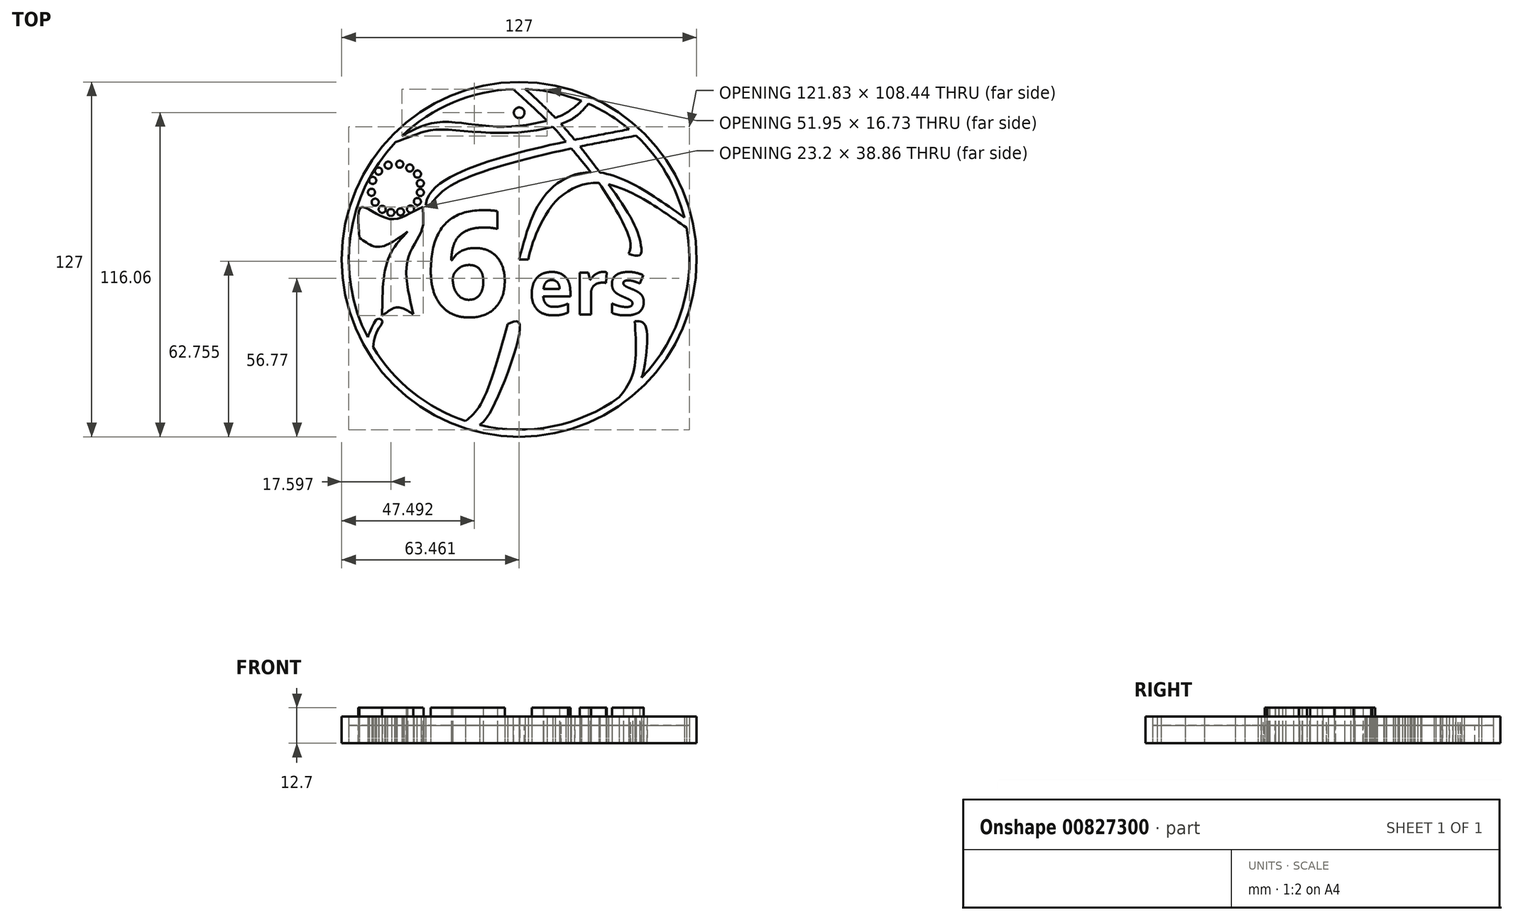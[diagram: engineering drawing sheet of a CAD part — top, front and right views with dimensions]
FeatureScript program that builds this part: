
annotation { "Feature Type Name" : "Feature", "Feature Type Description" : "" }
export const myFeature = defineFeature(function(context is Context, id is Id, definition is map)
    precondition{}
    {
        {
            var Q0;
            Q0=qCreatedBy(makeId("Top.planeOp"),FACE);
            var sketch = newSketch(context, id + "F0", { "sketchPlane" : qUnion([Q0])});
            skCircle(sketch, "E0", {"center": v(0, 0) * mm, "radius": 63.5 * mm});
            skCircle(sketch, "E1", {"center": v(0, 0) * mm, "radius": 60.96 * mm});
            skFitSpline(sketch, "E2", {"points": [v(-54.2, -27.9) * mm, v(-52.23, -23.42) * mm, v(-50.53, -21.33) * mm, v(-49.01, -22.09) * mm, v(-50.72, -25.5) * mm, v(-52.26, -31.38) * mm], "startDerivative": vector(8.28, 20.2) * mm, "endDerivative": vector(-3.3, -23.9) * mm});
            skFitSpline(sketch, "E3", {"points": [v(-49.01, -20.18) * mm, v(-43.9, -17.16) * mm, v(-37.82, -19.62) * mm], "startDerivative": vector(10.4, 7.01) * mm, "endDerivative": vector(11.94, -7.2) * mm});
            skFitSpline(sketch, "E4", {"points": [v(-37.82, -19.62) * mm, v(-39.86, 0) * mm, v(-34.6, 11.28) * mm, v(-34.47, 18.69) * mm], "startDerivative": vector(-12.1, 50.15) * mm, "endDerivative": vector(0.96, 26.71) * mm});
            skFitSpline(sketch, "E5", {"points": [v(-34.47, 18.69) * mm, v(-46.5, 14.5) * mm, v(-56.48, 18.69) * mm, v(-57.22, 7.7) * mm], "startDerivative": vector(-38.35, -14.44) * mm, "endDerivative": vector(0.93, -47.09) * mm});
            skFitSpline(sketch, "E6", {"points": [v(-57.22, 7.7) * mm, v(-50.53, 4.46) * mm, v(-39.86, 9.95) * mm], "startDerivative": vector(14.43, -9.54) * mm, "endDerivative": vector(19.87, 14.21) * mm});
            skFitSpline(sketch, "E7", {"points": [v(-39.86, 9.95) * mm, v(-46.93, 0) * mm, v(-49.01, -20.18) * mm], "startDerivative": vector(-18.63, -19.86) * mm, "endDerivative": vector(-0.32, -38.2) * mm});
            skCircle(sketch, "E8", {"center": v(-42.48, 17) * mm, "radius": 1.27 * mm});
            skCircle(sketch, "E9", {"center": v(-38.87, 18.01) * mm, "radius": 1.27 * mm});
            skCircle(sketch, "E10", {"center": v(-36.4, 20.69) * mm, "radius": 1.27 * mm});
            skCircle(sketch, "E11", {"center": v(-35.38, 23.93) * mm, "radius": 1.27 * mm});
            skCircle(sketch, "E12", {"center": v(-35.38, 27.2) * mm, "radius": 1.27 * mm});
            skCircle(sketch, "E13", {"center": v(-36.4, 30.53) * mm, "radius": 1.27 * mm});
            skCircle(sketch, "E14", {"center": v(-39.15, 32.7) * mm, "radius": 1.27 * mm});
            skCircle(sketch, "E15", {"center": v(-42.73, 34.07) * mm, "radius": 1.27 * mm});
            skCircle(sketch, "E16", {"center": v(-46.86, 33.7) * mm, "radius": 1.27 * mm});
            skCircle(sketch, "E17", {"center": v(-50.3, 31.59) * mm, "radius": 1.27 * mm});
            skCircle(sketch, "E18", {"center": v(-52.42, 28.24) * mm, "radius": 1.27 * mm});
            skCircle(sketch, "E19", {"center": v(-52.85, 23.99) * mm, "radius": 1.27 * mm});
            skCircle(sketch, "E20", {"center": v(-51.53, 20.48) * mm, "radius": 1.27 * mm});
            skCircle(sketch, "E21", {"center": v(-49, 17.9) * mm, "radius": 1.27 * mm});
            skCircle(sketch, "E22", {"center": v(-45.92, 16.77) * mm, "radius": 1.27 * mm});
            skPoint(sketch, "E23", {"position": v(-16.13, 18.69) * mm});
            skPoint(sketch, "E24", {"position": v(-16.13, -20.18) * mm});
            skText(sketch, "E25", { "text": "6", "fontName": "OpenSans-Bold.ttf"});
            skText(sketch, "E26", { "text": "ers", "fontName": "OpenSans-Bold.ttf"});
            skFitSpline(sketch, "E27", {"points": [v(-31.72, 19.4) * mm, v(-15.34, 30.53) * mm, v(41.92, 44.25) * mm], "startDerivative": vector(25.64, 42.91) * mm, "endDerivative": vector(102.82, 18.21) * mm});
            skFitSpline(sketch, "E28", {"points": [v(-33.46, 19.4) * mm, v(-22.43, 30.53) * mm, v(6.43, 39.84) * mm, v(39.36, 46.55) * mm], "startDerivative": vector(8.52, 60) * mm, "endDerivative": vector(83.39, 15.7) * mm});
            skFitSpline(sketch, "E29", {"points": [v(-41.99, 44.2) * mm, v(-28.87, 49.08) * mm, v(-7.34, 47.48) * mm, v(14.98, 51.47) * mm, v(22.29, 56.74) * mm], "startDerivative": vector(52.87, 28.6) * mm, "endDerivative": vector(31.88, 29.74) * mm});
            skFitSpline(sketch, "E30", {"points": [v(-44.2, 41.97) * mm, v(-37.5, 44.52) * mm, v(-29.62, 46.43) * mm, v(-7.1, 45.23) * mm, v(17.47, 49.47) * mm, v(24.76, 55.7) * mm], "startDerivative": vector(46.42, 16.58) * mm, "endDerivative": vector(33.1, 40.53) * mm});
            skFitSpline(sketch, "E31", {"points": [v(0, 0) * mm, v(9.53, 23.28) * mm, v(28.02, 31.17) * mm, v(59.1, 14.98) * mm], "startDerivative": vector(20.8, 79.75) * mm, "endDerivative": vector(83.63, -59.85) * mm});
            skFitSpline(sketch, "E32", {"points": [v(3.26, 0) * mm, v(5.48, 7.5) * mm, v(13.6, 21.25) * mm, v(28.47, 27.34) * mm, v(47.19, 19.9) * mm, v(59.9, 11.32) * mm], "startDerivative": vector(9.3, 47.2) * mm, "endDerivative": vector(57.56, -41.12) * mm});
            skFitSpline(sketch, "E33", {"points": [v(0, 0) * mm, v(3.26, 0) * mm], "startDerivative": vector(3.54, 0) * mm, "endDerivative": vector(3.54, 0) * mm});
            skFitSpline(sketch, "E34", {"points": [v(-33.46, 19.4) * mm, v(-31.72, 19.4) * mm], "startDerivative": vector(1.74, 0) * mm, "endDerivative": vector(1.74, 0) * mm});
            skFitSpline(sketch, "E35", {"points": [v(35.83, -49.32) * mm, v(40.75, -40.8) * mm, v(41.39, -22.1) * mm], "startDerivative": vector(13.93, 17.74) * mm, "endDerivative": vector(-1.97, 35.73) * mm});
            skFitSpline(sketch, "E36", {"points": [v(43.8, -42.4) * mm, v(44.74, -38.89) * mm, v(45.05, -23.58) * mm, v(41.39, -22.1) * mm], "startDerivative": vector(3.64, 9.81) * mm, "endDerivative": vector(-17.03, 0.06) * mm});
            skFitSpline(sketch, "E37", {"points": [v(39.16, 1.93) * mm, v(39.63, 6.7) * mm, v(28.47, 27.34) * mm, v(18.66, 39.7) * mm, v(12.06, 47.5) * mm, v(-2.14, 60.92) * mm], "startDerivative": vector(11.87, 33.04) * mm, "endDerivative": vector(-66.74, 59.9) * mm});
            skFitSpline(sketch, "E38", {"points": [v(2.14, 60.92) * mm, v(6.47, 57.09) * mm, v(14.98, 48.42) * mm, v(21.77, 40.37) * mm, v(32, 26.84) * mm, v(41.07, 12.77) * mm, v(43.46, 5.6) * mm, v(43.3, 1.6) * mm, v(39.16, 1.93) * mm], "startDerivative": vector(39.37, -33.43) * mm, "endDerivative": vector(-60.68, 17.03) * mm});
            skFitSpline(sketch, "E39", {"points": [v(-19.17, -57.87) * mm, v(-13.98, -52.18) * mm, v(-4.12, -23.17) * mm], "startDerivative": vector(15.65, 12.5) * mm, "endDerivative": vector(14.54, 52.37) * mm});
            skFitSpline(sketch, "E40", {"points": [v(-14.15, -59.3) * mm, v(-9.8, -53.7) * mm, v(0, -22.8) * mm, v(-4.12, -23.17) * mm], "startDerivative": vector(14.17, 11.52) * mm, "endDerivative": vector(-26.92, -12.48) * mm});
            const initialGuessF0  = {"E25": [-0.03346, -0.02029, 1, 0, 0.0378], "E26": [0.00326, -0.01978, 1, 0, 0.01978]};
            skSetInitialGuess(sketch, initialGuessF0);
            skSolve(sketch);
        }
        {
            var Q0;
            Q0=makeQuery(id+"F0.imprint","IMPRINT",FACE,{"disambiguationData":[TD([[makeQuery(id+"F0.imprint","IMPRINT",EDGE,{"derivedFrom":sQuery(id+"F0.wireOp",EDGE,"E0")}),1.0]])]});
            var Q1;
            Q1=makeQuery(id+"F0.imprint","IMPRINT",FACE,{"disambiguationData":[TD([[makeQuery(id+"F0.imprint","IMPRINT",EDGE,{"derivedFrom":sQuery(id+"F0.wireOp",EDGE,"E8")}),1.0]])]});
            var Q2;
            Q2=makeQuery(id+"F0.imprint","IMPRINT",FACE,{"disambiguationData":[TD([[makeQuery(id+"F0.imprint","IMPRINT",EDGE,{"derivedFrom":sQuery(id+"F0.wireOp",EDGE,"E9")}),1.0]])]});
            var Q3;
            Q3=makeQuery(id+"F0.imprint","IMPRINT",FACE,{"disambiguationData":[TD([[makeQuery(id+"F0.imprint","IMPRINT",EDGE,{"derivedFrom":sQuery(id+"F0.wireOp",EDGE,"E11")}),1.0]])]});
            var Q4;
            Q4=makeQuery(id+"F0.imprint","IMPRINT",FACE,{"disambiguationData":[TD([[makeQuery(id+"F0.imprint","IMPRINT",EDGE,{"derivedFrom":sQuery(id+"F0.wireOp",EDGE,"E10")}),1.0]])]});
            var Q5;
            Q5=makeQuery(id+"F0.imprint","IMPRINT",FACE,{"disambiguationData":[TD([[makeQuery(id+"F0.imprint","IMPRINT",EDGE,{"derivedFrom":sQuery(id+"F0.wireOp",EDGE,"E12")}),1.0]])]});
            var Q6;
            Q6=makeQuery(id+"F0.imprint","IMPRINT",FACE,{"disambiguationData":[TD([[makeQuery(id+"F0.imprint","IMPRINT",EDGE,{"derivedFrom":sQuery(id+"F0.wireOp",EDGE,"E13")}),1.0]])]});
            var Q7;
            Q7=makeQuery(id+"F0.imprint","IMPRINT",FACE,{"disambiguationData":[TD([[makeQuery(id+"F0.imprint","IMPRINT",EDGE,{"derivedFrom":sQuery(id+"F0.wireOp",EDGE,"E14")}),1.0]])]});
            var Q8;
            Q8=makeQuery(id+"F0.imprint","IMPRINT",FACE,{"disambiguationData":[TD([[makeQuery(id+"F0.imprint","IMPRINT",EDGE,{"derivedFrom":sQuery(id+"F0.wireOp",EDGE,"E15")}),1.0]])]});
            var Q9;
            Q9=makeQuery(id+"F0.imprint","IMPRINT",FACE,{"disambiguationData":[TD([[makeQuery(id+"F0.imprint","IMPRINT",EDGE,{"derivedFrom":sQuery(id+"F0.wireOp",EDGE,"E16")}),1.0]])]});
            var Q10;
            Q10=makeQuery(id+"F0.imprint","IMPRINT",FACE,{"disambiguationData":[TD([[makeQuery(id+"F0.imprint","IMPRINT",EDGE,{"derivedFrom":sQuery(id+"F0.wireOp",EDGE,"E17")}),1.0]])]});
            var Q11;
            Q11=makeQuery(id+"F0.imprint","IMPRINT",FACE,{"disambiguationData":[TD([[makeQuery(id+"F0.imprint","IMPRINT",EDGE,{"derivedFrom":sQuery(id+"F0.wireOp",EDGE,"E18")}),1.0]])]});
            var Q12;
            Q12=makeQuery(id+"F0.imprint","IMPRINT",FACE,{"disambiguationData":[TD([[makeQuery(id+"F0.imprint","IMPRINT",EDGE,{"derivedFrom":sQuery(id+"F0.wireOp",EDGE,"E19")}),1.0]])]});
            var Q13;
            Q13=makeQuery(id+"F0.imprint","IMPRINT",FACE,{"disambiguationData":[TD([[makeQuery(id+"F0.imprint","IMPRINT",EDGE,{"derivedFrom":sQuery(id+"F0.wireOp",EDGE,"E20")}),1.0]])]});
            var Q14;
            Q14=makeQuery(id+"F0.imprint","IMPRINT",FACE,{"disambiguationData":[TD([[makeQuery(id+"F0.imprint","IMPRINT",EDGE,{"derivedFrom":sQuery(id+"F0.wireOp",EDGE,"E21")}),1.0]])]});
            var Q15;
            Q15=makeQuery(id+"F0.imprint","IMPRINT",FACE,{"disambiguationData":[TD([[makeQuery(id+"F0.imprint","IMPRINT",EDGE,{"derivedFrom":sQuery(id+"F0.wireOp",EDGE,"E22")}),1.0]])]});
            var Q16;
            {var subQ0=sQuery(id+"F0.wireOp",EDGE,"E34");Q16=makeQuery(id+"F0.imprint","IMPRINT",FACE,{"disambiguationData":[TD([[makeQuery(id+"F0.imprint","IMPRINT",EDGE,{"derivedFrom":subQ0}),1.0]])]});}
            var Q17;
            {var subQ0=sQuery(id+"F0.wireOp",EDGE,"E29");var subQ1=sQuery(id+"F0.wireOp",EDGE,"E1");var subQ2=makeQuery(id+"F0.imprint","INTERSECT",VERTEX,{"disambiguationData":[OD(0.0)],"derivedFrom":[subQ1,subQ0]});Q17=makeQuery(id+"F0.imprint","IMPRINT",FACE,{"disambiguationData":[TD([[makeQuery(id+"F0.imprint","IMPRINT",EDGE,{"disambiguationData":[TD([[subQ2,-1.0]])],"derivedFrom":subQ1}),1.0]])]});}
            var Q18;
            {var subQ0=sQuery(id+"F0.wireOp",EDGE,"E37");var subQ1=sQuery(id+"F0.wireOp",EDGE,"E29");var subQ2=makeQuery(id+"F0.imprint","INTERSECT",VERTEX,{"derivedFrom":[subQ1,subQ0]});Q18=makeQuery(id+"F0.imprint","IMPRINT",FACE,{"disambiguationData":[TD([[makeQuery(id+"F0.imprint","IMPRINT",EDGE,{"disambiguationData":[TD([[subQ2,-1.0]])],"derivedFrom":subQ1}),-1.0]])]});}
            var Q19;
            {var subQ0=sQuery(id+"F0.wireOp",EDGE,"E37");var subQ1=sQuery(id+"F0.wireOp",EDGE,"E1");var subQ2=makeQuery(id+"F0.imprint","INTERSECT",VERTEX,{"derivedFrom":[subQ1,subQ0]});Q19=makeQuery(id+"F0.imprint","IMPRINT",FACE,{"disambiguationData":[TD([[makeQuery(id+"F0.imprint","IMPRINT",EDGE,{"disambiguationData":[TD([[subQ2,1.0]])],"derivedFrom":subQ1}),1.0]])]});}
            var Q20;
            {var subQ0=sQuery(id+"F0.wireOp",EDGE,"E29");var subQ1=sQuery(id+"F0.wireOp",EDGE,"E1");var subQ2=makeQuery(id+"F0.imprint","INTERSECT",VERTEX,{"disambiguationData":[OD(1.0)],"derivedFrom":[subQ1,subQ0]});Q20=makeQuery(id+"F0.imprint","IMPRINT",FACE,{"disambiguationData":[TD([[makeQuery(id+"F0.imprint","IMPRINT",EDGE,{"disambiguationData":[TD([[subQ2,1.0]])],"derivedFrom":subQ1}),1.0]])]});}
            var Q21;
            {var subQ0=sQuery(id+"F0.wireOp",EDGE,"E37");var subQ1=sQuery(id+"F0.wireOp",EDGE,"E28");var subQ2=makeQuery(id+"F0.imprint","INTERSECT",VERTEX,{"derivedFrom":[subQ1,subQ0]});Q21=makeQuery(id+"F0.imprint","IMPRINT",FACE,{"disambiguationData":[TD([[makeQuery(id+"F0.imprint","IMPRINT",EDGE,{"disambiguationData":[TD([[subQ2,-1.0]])],"derivedFrom":subQ1}),1.0]])]});}
            var Q22;
            {var subQ0=sQuery(id+"F0.wireOp",EDGE,"E37");var subQ1=sQuery(id+"F0.wireOp",EDGE,"E27");var subQ2=makeQuery(id+"F0.imprint","INTERSECT",VERTEX,{"derivedFrom":[subQ1,subQ0]});Q22=makeQuery(id+"F0.imprint","IMPRINT",FACE,{"disambiguationData":[TD([[makeQuery(id+"F0.imprint","IMPRINT",EDGE,{"disambiguationData":[TD([[subQ2,-1.0]])],"derivedFrom":subQ1}),1.0]])]});}
            var Q23;
            {var subQ0=sQuery(id+"F0.wireOp",EDGE,"E27");var subQ1=sQuery(id+"F0.wireOp",EDGE,"E1");var subQ2=makeQuery(id+"F0.imprint","INTERSECT",VERTEX,{"derivedFrom":[subQ1,subQ0]});Q23=makeQuery(id+"F0.imprint","IMPRINT",FACE,{"disambiguationData":[TD([[makeQuery(id+"F0.imprint","IMPRINT",EDGE,{"disambiguationData":[TD([[subQ2,-1.0]])],"derivedFrom":subQ1}),1.0]])]});}
            var Q24;
            {var subQ0=sQuery(id+"F0.wireOp",EDGE,"E37");var subQ1=sQuery(id+"F0.wireOp",EDGE,"E27");var subQ2=makeQuery(id+"F0.imprint","INTERSECT",VERTEX,{"derivedFrom":[subQ1,subQ0]});Q24=makeQuery(id+"F0.imprint","IMPRINT",FACE,{"disambiguationData":[TD([[makeQuery(id+"F0.imprint","IMPRINT",EDGE,{"disambiguationData":[TD([[subQ2,-1.0]])],"derivedFrom":subQ1}),-1.0]])]});}
            var Q25;
            {var subQ0=sQuery(id+"F0.wireOp",EDGE,"E37");var subQ1=sQuery(id+"F0.wireOp",EDGE,"E31");var subQ2=makeQuery(id+"F0.imprint","INTERSECT",VERTEX,{"derivedFrom":[subQ1,subQ0]});Q25=makeQuery(id+"F0.imprint","IMPRINT",FACE,{"disambiguationData":[TD([[makeQuery(id+"F0.imprint","IMPRINT",EDGE,{"disambiguationData":[TD([[subQ2,-1.0]])],"derivedFrom":subQ1}),-1.0]])]});}
            var Q26;
            {var subQ0=sQuery(id+"F0.wireOp",EDGE,"E31");var subQ1=sQuery(id+"F0.wireOp",EDGE,"E1");var subQ2=makeQuery(id+"F0.imprint","INTERSECT",VERTEX,{"derivedFrom":[subQ1,subQ0]});Q26=makeQuery(id+"F0.imprint","IMPRINT",FACE,{"disambiguationData":[TD([[makeQuery(id+"F0.imprint","IMPRINT",EDGE,{"disambiguationData":[TD([[subQ2,1.0]])],"derivedFrom":subQ1}),1.0]])]});}
            var Q27;
            {var subQ0=sQuery(id+"F0.wireOp",EDGE,"E33");Q27=makeQuery(id+"F0.imprint","IMPRINT",FACE,{"disambiguationData":[TD([[makeQuery(id+"F0.imprint","IMPRINT",EDGE,{"derivedFrom":subQ0}),1.0]])]});}
            var Q28;
            {var subQ0=sQuery(id+"F0.wireOp",EDGE,"E2");Q28=makeQuery(id+"F0.imprint","IMPRINT",FACE,{"disambiguationData":[TD([[makeQuery(id+"F0.imprint","IMPRINT",EDGE,{"derivedFrom":subQ0}),-1.0]])]});}
            var Q29;
            {var subQ0=sQuery(id+"F0.wireOp",EDGE,"E39");Q29=makeQuery(id+"F0.imprint","IMPRINT",FACE,{"disambiguationData":[TD([[makeQuery(id+"F0.imprint","IMPRINT",EDGE,{"derivedFrom":subQ0}),-1.0]])]});}
            var Q30;
            {var subQ0=sQuery(id+"F0.wireOp",EDGE,"E35");Q30=makeQuery(id+"F0.imprint","IMPRINT",FACE,{"disambiguationData":[TD([[makeQuery(id+"F0.imprint","IMPRINT",EDGE,{"derivedFrom":subQ0}),-1.0]])]});}
            var Q31;
            {var subQ0=sQuery(id+"F0.wireOp",EDGE,"E37");var subQ1=sQuery(id+"F0.wireOp",EDGE,"E32");var subQ2=makeQuery(id+"F0.imprint","INTERSECT",VERTEX,{"derivedFrom":[subQ1,subQ0]});Q31=makeQuery(id+"F0.imprint","IMPRINT",FACE,{"disambiguationData":[TD([[makeQuery(id+"F0.imprint","IMPRINT",EDGE,{"disambiguationData":[TD([[subQ2,-1.0]])],"derivedFrom":subQ1}),-1.0]])]});}
            extrude(context, id + "F1", {"entities" : qUnion([Q0, Q1, Q2, Q3, Q4, Q5, Q6, Q7, Q8, Q9, Q10, Q11, Q12, Q13, Q14, Q15, Q16, Q17, Q18, Q19, Q20, Q21, Q22, Q23, Q24, Q25, Q26, Q27, Q28, Q29, Q30, Q31]), "depth" : 9.52 * mm, "offsetDistance" : 25.4 * mm});
        }
        {
            var Q0;
            Q0=makeQuery(id+"F0.imprint","IMPRINT",FACE,{"disambiguationData":[TD([[makeQuery(id+"F0.imprint","IMPRINT",EDGE,{"derivedFrom":sQuery(id+"F0.wireOp",EDGE,"E25.sketch_text.stroke-17")}),1.0]])]});
            var Q1;
            {var subQ6=sQuery(id+"F0.wireOp",EDGE,"E2");Q1=makeQuery(id+"F0.imprint","IMPRINT",FACE,{"disambiguationData":[TD([[makeQuery(id+"F0.imprint","IMPRINT",EDGE,{"derivedFrom":subQ6}),1.0]])]});}
            var Q2;
            {var subQ0=sQuery(id+"F0.wireOp",EDGE,"E27");var subQ1=sQuery(id+"F0.wireOp",EDGE,"E1");var subQ2=makeQuery(id+"F0.imprint","INTERSECT",VERTEX,{"derivedFrom":[subQ1,subQ0]});Q2=makeQuery(id+"F0.imprint","IMPRINT",FACE,{"disambiguationData":[TD([[makeQuery(id+"F0.imprint","IMPRINT",EDGE,{"disambiguationData":[TD([[subQ2,1.0]])],"derivedFrom":subQ1}),1.0]])]});}
            var Q3;
            {var subQ0=sQuery(id+"F0.wireOp",EDGE,"E28");var subQ1=sQuery(id+"F0.wireOp",EDGE,"E1");var subQ2=makeQuery(id+"F0.imprint","INTERSECT",VERTEX,{"derivedFrom":[subQ1,subQ0]});Q3=makeQuery(id+"F0.imprint","IMPRINT",FACE,{"disambiguationData":[TD([[makeQuery(id+"F0.imprint","IMPRINT",EDGE,{"disambiguationData":[TD([[subQ2,-1.0]])],"derivedFrom":subQ1}),1.0]])]});}
            var Q4;
            {var subQ0=sQuery(id+"F0.wireOp",EDGE,"E29");var subQ1=sQuery(id+"F0.wireOp",EDGE,"E1");var subQ2=makeQuery(id+"F0.imprint","INTERSECT",VERTEX,{"disambiguationData":[OD(1.0)],"derivedFrom":[subQ1,subQ0]});Q4=makeQuery(id+"F0.imprint","IMPRINT",FACE,{"disambiguationData":[TD([[makeQuery(id+"F0.imprint","IMPRINT",EDGE,{"disambiguationData":[TD([[subQ2,-1.0]])],"derivedFrom":subQ1}),1.0]])]});}
            var Q5;
            {var subQ0=sQuery(id+"F0.wireOp",EDGE,"E29");var subQ1=sQuery(id+"F0.wireOp",EDGE,"E1");var subQ2=makeQuery(id+"F0.imprint","INTERSECT",VERTEX,{"disambiguationData":[OD(0.0)],"derivedFrom":[subQ1,subQ0]});Q5=makeQuery(id+"F0.imprint","IMPRINT",FACE,{"disambiguationData":[TD([[makeQuery(id+"F0.imprint","IMPRINT",EDGE,{"disambiguationData":[TD([[subQ2,1.0]])],"derivedFrom":subQ1}),1.0]])]});}
            var Q6;
            Q6=makeQuery(id+"F0.imprint","IMPRINT",FACE,{"disambiguationData":[TD([[makeQuery(id+"F0.imprint","IMPRINT",EDGE,{"derivedFrom":sQuery(id+"F0.wireOp",EDGE,"E26.sketch_text.stroke-0")}),1.0]])]});
            extrude(context, id + "F2", {"entities" : qUnion([Q0, Q1, Q2, Q3, Q4, Q5, Q6]), "depth" : 6.35 * mm, "offsetDistance" : 25.4 * mm});
        }
        {
            var Q0;
            Q0=makeQuery(id+"F0.imprint","IMPRINT",FACE,{"disambiguationData":[TD([[makeQuery(id+"F0.imprint","IMPRINT",EDGE,{"derivedFrom":sQuery(id+"F0.wireOp",EDGE,"E3")}),1.0]])]});
            var Q1;
            Q1=makeQuery(id+"F0.imprint","IMPRINT",FACE,{"disambiguationData":[TD([[makeQuery(id+"F0.imprint","IMPRINT",EDGE,{"derivedFrom":sQuery(id+"F0.wireOp",EDGE,"E25.sketch_text.stroke-0")}),-1.0]])]});
            var Q2;
            Q2=makeQuery(id+"F0.imprint","IMPRINT",FACE,{"disambiguationData":[TD([[makeQuery(id+"F0.imprint","IMPRINT",EDGE,{"derivedFrom":sQuery(id+"F0.wireOp",EDGE,"E26.sketch_text.stroke-0")}),-1.0]])]});
            var Q3;
            Q3=makeQuery(id+"F0.imprint","IMPRINT",FACE,{"disambiguationData":[TD([[makeQuery(id+"F0.imprint","IMPRINT",EDGE,{"derivedFrom":sQuery(id+"F0.wireOp",EDGE,"E26.sketch_text.stroke-20")}),-1.0]])]});
            var Q4;
            Q4=makeQuery(id+"F0.imprint","IMPRINT",FACE,{"disambiguationData":[TD([[makeQuery(id+"F0.imprint","IMPRINT",EDGE,{"derivedFrom":sQuery(id+"F0.wireOp",EDGE,"E26.sketch_text.stroke-33")}),-1.0]])]});
            extrude(context, id + "F3", {"entities" : qUnion([Q0, Q1, Q2, Q3, Q4]), "depth" : 12.7 * mm, "offsetDistance" : 25.4 * mm});
        }
        {
            var Q0;
            Q0=makeQuery(id+"F2.opExtrude","CAP_FACE",FACE,{"disambiguationData":[OSD([sQuery(id+"F0.wireOp",EDGE,"E1"),sQuery(id+"F0.wireOp",EDGE,"E2"),sQuery(id+"F0.wireOp",EDGE,"E3"),sQuery(id+"F0.wireOp",EDGE,"E4"),sQuery(id+"F0.wireOp",EDGE,"E5"),sQuery(id+"F0.wireOp",EDGE,"E6"),sQuery(id+"F0.wireOp",EDGE,"E7"),sQuery(id+"F0.wireOp",EDGE,"E8"),sQuery(id+"F0.wireOp",EDGE,"E9"),sQuery(id+"F0.wireOp",EDGE,"E10"),sQuery(id+"F0.wireOp",EDGE,"E11"),sQuery(id+"F0.wireOp",EDGE,"E12"),sQuery(id+"F0.wireOp",EDGE,"E13"),sQuery(id+"F0.wireOp",EDGE,"E14"),sQuery(id+"F0.wireOp",EDGE,"E15"),sQuery(id+"F0.wireOp",EDGE,"E16"),sQuery(id+"F0.wireOp",EDGE,"E17"),sQuery(id+"F0.wireOp",EDGE,"E18"),sQuery(id+"F0.wireOp",EDGE,"E19"),sQuery(id+"F0.wireOp",EDGE,"E20"),sQuery(id+"F0.wireOp",EDGE,"E21"),sQuery(id+"F0.wireOp",EDGE,"E22"),sQuery(id+"F0.wireOp",EDGE,"E25.sketch_text.stroke-0"),sQuery(id+"F0.wireOp",EDGE,"E25.sketch_text.stroke-1"),sQuery(id+"F0.wireOp",EDGE,"E25.sketch_text.stroke-2"),sQuery(id+"F0.wireOp",EDGE,"E25.sketch_text.stroke-3"),sQuery(id+"F0.wireOp",EDGE,"E25.sketch_text.stroke-4"),sQuery(id+"F0.wireOp",EDGE,"E25.sketch_text.stroke-5"),sQuery(id+"F0.wireOp",EDGE,"E25.sketch_text.stroke-6"),sQuery(id+"F0.wireOp",EDGE,"E25.sketch_text.stroke-7"),sQuery(id+"F0.wireOp",EDGE,"E25.sketch_text.stroke-8"),sQuery(id+"F0.wireOp",EDGE,"E25.sketch_text.stroke-9"),sQuery(id+"F0.wireOp",EDGE,"E25.sketch_text.stroke-10"),sQuery(id+"F0.wireOp",EDGE,"E25.sketch_text.stroke-11"),sQuery(id+"F0.wireOp",EDGE,"E25.sketch_text.stroke-12"),sQuery(id+"F0.wireOp",EDGE,"E25.sketch_text.stroke-13"),sQuery(id+"F0.wireOp",EDGE,"E25.sketch_text.stroke-14"),sQuery(id+"F0.wireOp",EDGE,"E25.sketch_text.stroke-15"),sQuery(id+"F0.wireOp",EDGE,"E25.sketch_text.stroke-16"),sQuery(id+"F0.wireOp",EDGE,"E26.sketch_text.stroke-5"),sQuery(id+"F0.wireOp",EDGE,"E26.sketch_text.stroke-6"),sQuery(id+"F0.wireOp",EDGE,"E26.sketch_text.stroke-7"),sQuery(id+"F0.wireOp",EDGE,"E26.sketch_text.stroke-8"),sQuery(id+"F0.wireOp",EDGE,"E26.sketch_text.stroke-9"),sQuery(id+"F0.wireOp",EDGE,"E26.sketch_text.stroke-10"),sQuery(id+"F0.wireOp",EDGE,"E26.sketch_text.stroke-11"),sQuery(id+"F0.wireOp",EDGE,"E26.sketch_text.stroke-12"),sQuery(id+"F0.wireOp",EDGE,"E26.sketch_text.stroke-13"),sQuery(id+"F0.wireOp",EDGE,"E26.sketch_text.stroke-14"),sQuery(id+"F0.wireOp",EDGE,"E26.sketch_text.stroke-15"),sQuery(id+"F0.wireOp",EDGE,"E26.sketch_text.stroke-16"),sQuery(id+"F0.wireOp",EDGE,"E26.sketch_text.stroke-17"),sQuery(id+"F0.wireOp",EDGE,"E26.sketch_text.stroke-18"),sQuery(id+"F0.wireOp",EDGE,"E26.sketch_text.stroke-19"),sQuery(id+"F0.wireOp",EDGE,"E26.sketch_text.stroke-20"),sQuery(id+"F0.wireOp",EDGE,"E26.sketch_text.stroke-21"),sQuery(id+"F0.wireOp",EDGE,"E26.sketch_text.stroke-22"),sQuery(id+"F0.wireOp",EDGE,"E26.sketch_text.stroke-23"),sQuery(id+"F0.wireOp",EDGE,"E26.sketch_text.stroke-24"),sQuery(id+"F0.wireOp",EDGE,"E26.sketch_text.stroke-25"),sQuery(id+"F0.wireOp",EDGE,"E26.sketch_text.stroke-26"),sQuery(id+"F0.wireOp",EDGE,"E26.sketch_text.stroke-27"),sQuery(id+"F0.wireOp",EDGE,"E26.sketch_text.stroke-28"),sQuery(id+"F0.wireOp",EDGE,"E26.sketch_text.stroke-29"),sQuery(id+"F0.wireOp",EDGE,"E26.sketch_text.stroke-30"),sQuery(id+"F0.wireOp",EDGE,"E26.sketch_text.stroke-31"),sQuery(id+"F0.wireOp",EDGE,"E26.sketch_text.stroke-32"),sQuery(id+"F0.wireOp",EDGE,"E26.sketch_text.stroke-33"),sQuery(id+"F0.wireOp",EDGE,"E26.sketch_text.stroke-34"),sQuery(id+"F0.wireOp",EDGE,"E26.sketch_text.stroke-35"),sQuery(id+"F0.wireOp",EDGE,"E26.sketch_text.stroke-36"),sQuery(id+"F0.wireOp",EDGE,"E26.sketch_text.stroke-37"),sQuery(id+"F0.wireOp",EDGE,"E26.sketch_text.stroke-38"),sQuery(id+"F0.wireOp",EDGE,"E26.sketch_text.stroke-39"),sQuery(id+"F0.wireOp",EDGE,"E26.sketch_text.stroke-40"),sQuery(id+"F0.wireOp",EDGE,"E26.sketch_text.stroke-41"),sQuery(id+"F0.wireOp",EDGE,"E26.sketch_text.stroke-42"),sQuery(id+"F0.wireOp",EDGE,"E26.sketch_text.stroke-43"),sQuery(id+"F0.wireOp",EDGE,"E26.sketch_text.stroke-44"),sQuery(id+"F0.wireOp",EDGE,"E26.sketch_text.stroke-45"),sQuery(id+"F0.wireOp",EDGE,"E26.sketch_text.stroke-46"),sQuery(id+"F0.wireOp",EDGE,"E26.sketch_text.stroke-47"),sQuery(id+"F0.wireOp",EDGE,"E26.sketch_text.stroke-48"),sQuery(id+"F0.wireOp",EDGE,"E26.sketch_text.stroke-49"),sQuery(id+"F0.wireOp",EDGE,"E26.sketch_text.stroke-50"),sQuery(id+"F0.wireOp",EDGE,"E26.sketch_text.stroke-51"),sQuery(id+"F0.wireOp",EDGE,"E26.sketch_text.stroke-52"),sQuery(id+"F0.wireOp",EDGE,"E26.sketch_text.stroke-53"),sQuery(id+"F0.wireOp",EDGE,"E26.sketch_text.stroke-54"),sQuery(id+"F0.wireOp",EDGE,"E26.sketch_text.stroke-55"),sQuery(id+"F0.wireOp",EDGE,"E26.sketch_text.stroke-56"),sQuery(id+"F0.wireOp",EDGE,"E26.sketch_text.stroke-57"),sQuery(id+"F0.wireOp",EDGE,"E26.sketch_text.stroke-58"),sQuery(id+"F0.wireOp",EDGE,"E27"),sQuery(id+"F0.wireOp",EDGE,"E28"),sQuery(id+"F0.wireOp",EDGE,"E30"),sQuery(id+"F0.wireOp",EDGE,"E31"),sQuery(id+"F0.wireOp",EDGE,"E32"),sQuery(id+"F0.wireOp",EDGE,"E33"),sQuery(id+"F0.wireOp",EDGE,"E34"),sQuery(id+"F0.wireOp",EDGE,"E35"),sQuery(id+"F0.wireOp",EDGE,"E36"),sQuery(id+"F0.wireOp",EDGE,"E37"),sQuery(id+"F0.wireOp",EDGE,"E38"),sQuery(id+"F0.wireOp",EDGE,"E39"),sQuery(id+"F0.wireOp",EDGE,"E40")])],"isStart":false});
            var sketch = newSketch(context, id + "F4", { "sketchPlane" : qUnion([Q0])});
            skCircle(sketch, "E41", {"center": v(0, 52.48) * mm, "radius": 1.9 * mm});
            skSolve(sketch);
        }
        {
            var Q0;
            Q0=makeQuery(id+"F4.imprint","IMPRINT",FACE,{"disambiguationData":[TD([[makeQuery(id+"F4.imprint","IMPRINT",EDGE,{"derivedFrom":sQuery(id+"F4.wireOp",EDGE,"E41")}),1.0]])]});
            extrude(context, id + "F5", {"entities" : qUnion([Q0]), "operationType" : NewBodyOperationType.REMOVE, "oppositeDirection" : true, "depth" : 25.65 * mm, "offsetDistance" : 25.4 * mm});
        }
    });
